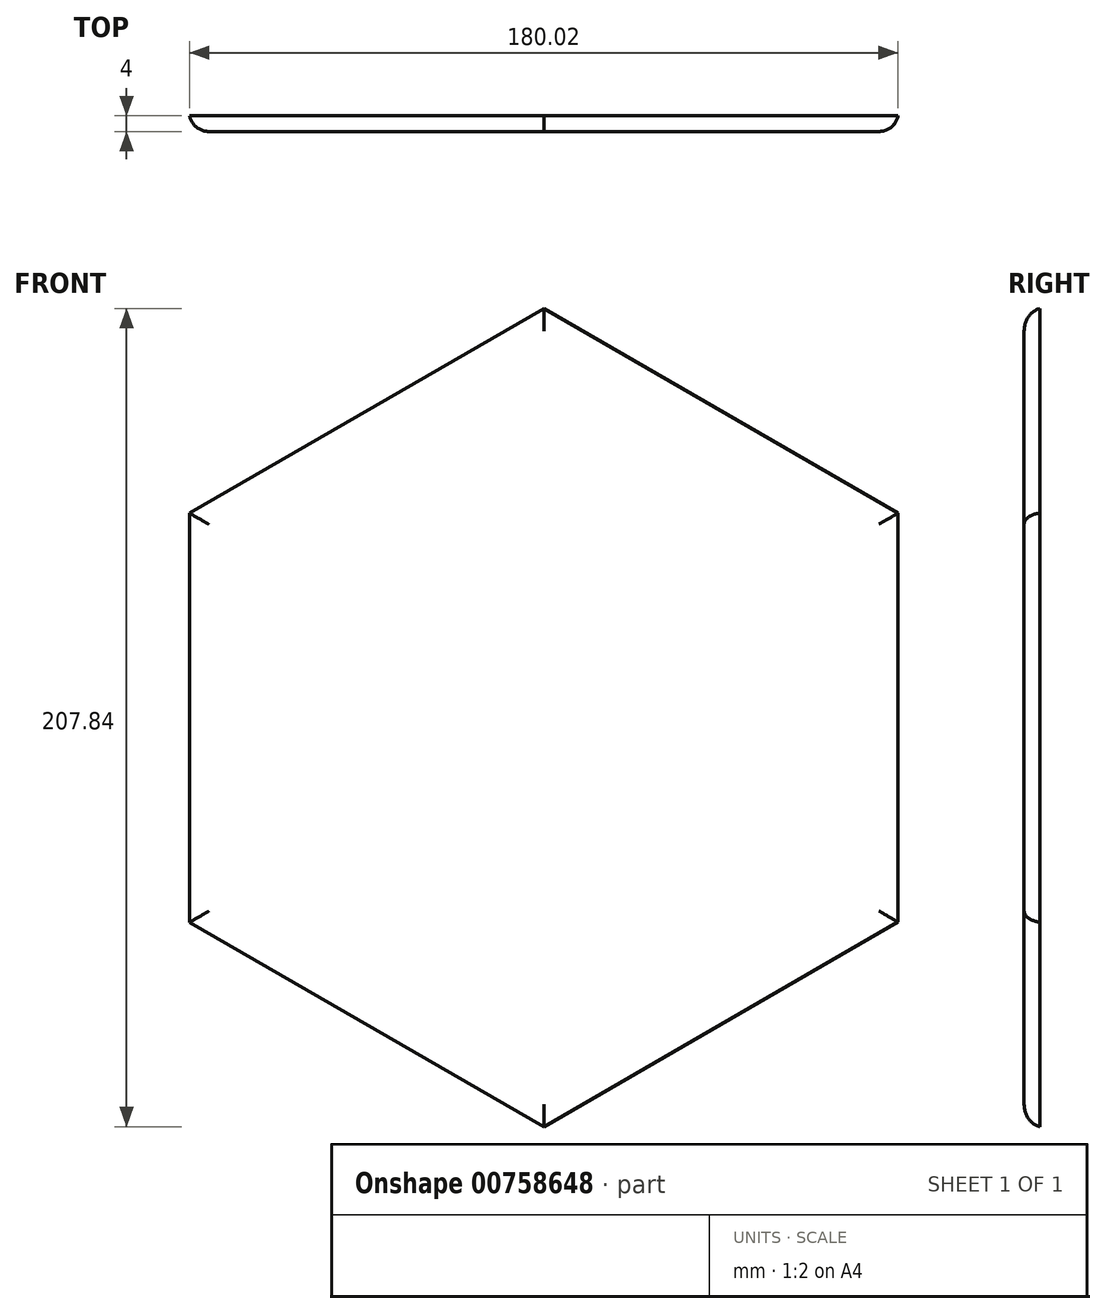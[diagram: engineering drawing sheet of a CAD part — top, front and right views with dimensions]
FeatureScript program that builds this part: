
annotation { "Feature Type Name" : "Feature", "Feature Type Description" : "" }
export const myFeature = defineFeature(function(context is Context, id is Id, definition is map)
    precondition{}
    {
        {
            var Q0;
            Q0=qCreatedBy(makeId("Front.planeOp"),FACE);
            var sketch = newSketch(context, id + "F0", { "sketchPlane" : qUnion([Q0])});
            skCircle(sketch, "E0.cCircle", {"center": v(0, 0) * mm, "radius": 90 * mm, "construction": true});
            skLineSegment(sketch, "E0.0", {"start": v(-0.01, 103.92) * mm, "end": v(90, 51.97) * mm});
            skLineSegment(sketch, "E0.1", {"start": v(90, 51.97) * mm, "end": v(90, -51.95) * mm});
            skLineSegment(sketch, "E0.2", {"start": v(90, -51.95) * mm, "end": v(0.01, -103.92) * mm});
            skLineSegment(sketch, "E0.3", {"start": v(0.01, -103.92) * mm, "end": v(-90, -51.97) * mm});
            skLineSegment(sketch, "E0.4", {"start": v(-90, -51.97) * mm, "end": v(-90, 51.95) * mm});
            skLineSegment(sketch, "E0.5", {"start": v(-90, 51.95) * mm, "end": v(-0.01, 103.92) * mm});
            skPoint(sketch, "E0.0.midPoint", {"position": v(44.99, 77.95) * mm});
            skSolve(sketch);
        }
        {
            var Q0;
            Q0=makeQuery(id+"F0.imprint","IMPRINT",FACE,{"disambiguationData":[TD([[makeQuery(id+"F0.imprint","IMPRINT",EDGE,{"derivedFrom":sQuery(id+"F0.wireOp",EDGE,"E0.0")}),-1.0]])]});
            extrude(context, id + "F1", {"entities" : qUnion([Q0]), "depth" : 4 * mm, "offsetDistance" : 25 * mm});
        }
        {
            var Q0;
            Q0=makeQuery(id+"F1.opExtrude","CAP_EDGE",EDGE,{"disambiguationData":[OSD([sQuery(id+"F0.wireOp",EDGE,"E0.4")])],"isStart":false});
            var Q1;
            Q1=makeQuery(id+"F1.opExtrude","CAP_EDGE",EDGE,{"disambiguationData":[OSD([sQuery(id+"F0.wireOp",EDGE,"E0.5")])],"isStart":false});
            var Q2;
            Q2=makeQuery(id+"F1.opExtrude","CAP_EDGE",EDGE,{"disambiguationData":[OSD([sQuery(id+"F0.wireOp",EDGE,"E0.0")])],"isStart":false});
            var Q3;
            Q3=makeQuery(id+"F1.opExtrude","CAP_EDGE",EDGE,{"disambiguationData":[OSD([sQuery(id+"F0.wireOp",EDGE,"E0.1")])],"isStart":false});
            var Q4;
            Q4=makeQuery(id+"F1.opExtrude","CAP_EDGE",EDGE,{"disambiguationData":[OSD([sQuery(id+"F0.wireOp",EDGE,"E0.2")])],"isStart":false});
            var Q5;
            Q5=makeQuery(id+"F1.opExtrude","CAP_EDGE",EDGE,{"disambiguationData":[OSD([sQuery(id+"F0.wireOp",EDGE,"E0.3")])],"isStart":false});
            fillet(context, id + "F2", {"entities" : qUnion([Q0, Q1, Q2, Q3, Q4, Q5]), "radius" : 5 * mm, "tangentPropagation" : true, "allowEdgeOverflow" : false});
        }
    });
